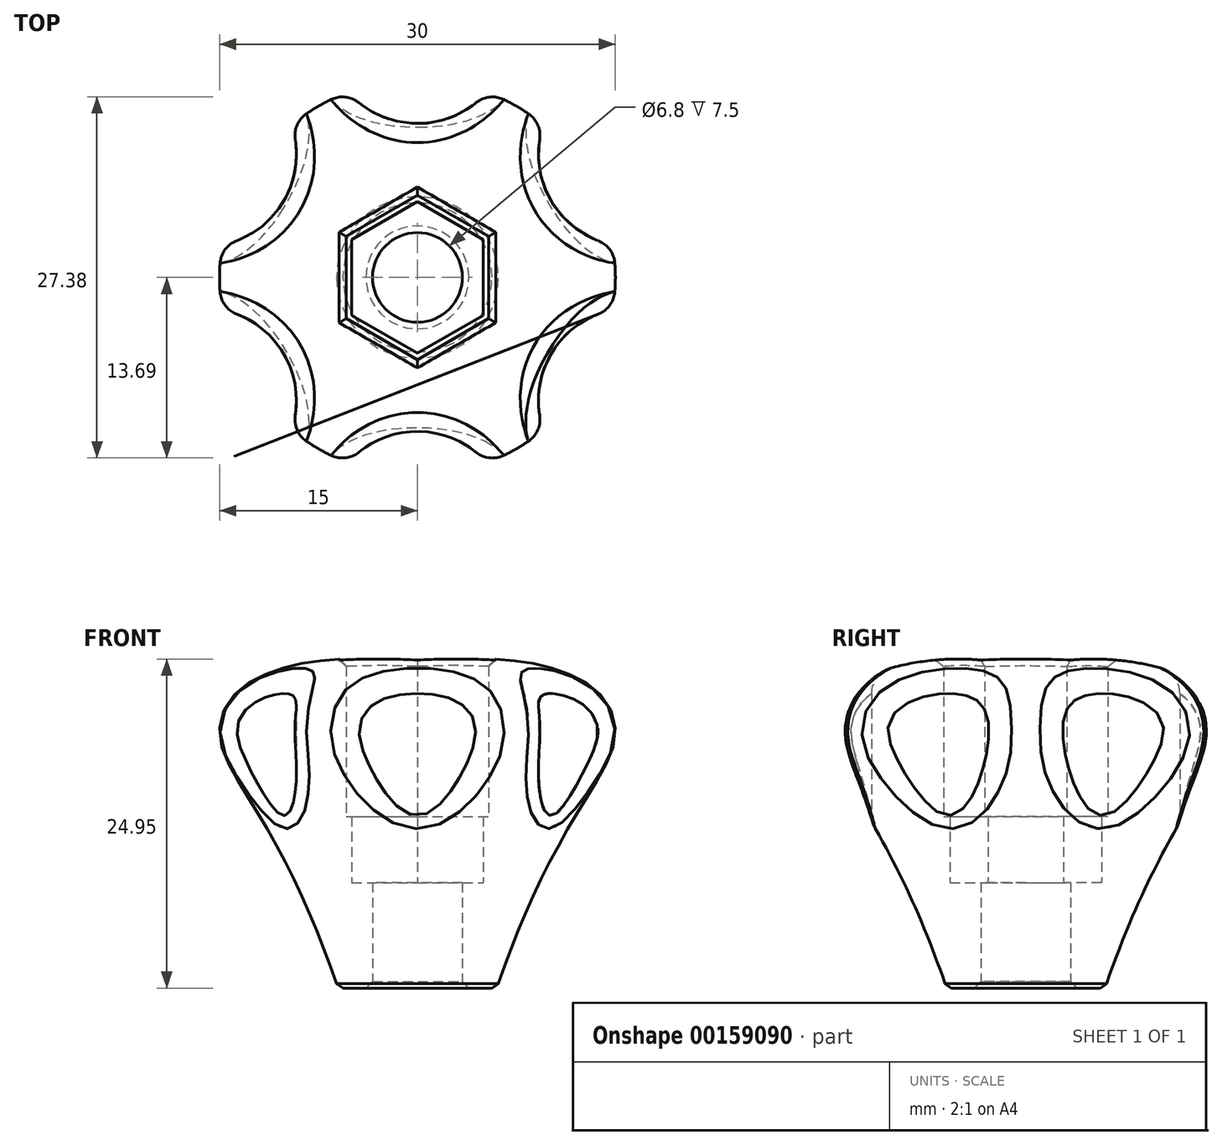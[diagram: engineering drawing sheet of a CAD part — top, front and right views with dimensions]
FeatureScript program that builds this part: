
annotation { "Feature Type Name" : "Feature", "Feature Type Description" : "" }
export const myFeature = defineFeature(function(context is Context, id is Id, definition is map)
    precondition{}
    {
        {
            var Q0;
            Q0=qCreatedBy(makeId("Right.planeOp"),FACE);
            var sketch = newSketch(context, id + "F0", { "sketchPlane" : qUnion([Q0])});
            skLineSegment(sketch, "E0", {"start": v(3.4, 25) * mm, "end": v(3.4, 0) * mm});
            skLineSegment(sketch, "E1", {"start": v(3.4, 0) * mm, "end": v(6, 0) * mm});
            skFitSpline(sketch, "E2", {"points": [v(6, 0) * mm, v(15, 19.47) * mm, v(3.4, 25) * mm], "startDerivative": vector(24.35, 70.88) * mm, "endDerivative": vector(-61.62, -0.98) * mm});
            skLineSegment(sketch, "E3", {"start": v(0, 0) * mm, "end": v(0, 25) * mm, "construction": true});
            skSolve(sketch);
        }
        {
            var Q0;
            Q0 = qSketchRegion(id + "F0", true);
            var Q1;
            Q1=sQuery(id+"F0.wireOp",EDGE,"E3");
            revolve(context, id + "F1", {"entities" : qUnion([Q0]), "axis" : qUnion([Q1]), "revolveType" : RevolveType.FULL});
        }
        {
            var Q0;
            Q0=qCreatedBy(makeId("Top.planeOp"),FACE);
            cPlane(context, id + "F2", {"entities" : qUnion([Q0]), "cplaneType" : CPlaneType.OFFSET, "offset" : 8 * mm, "width" : 150 * mm, "height" : 150 * mm});
        }
        {
            var Q0;
            Q0=qCreatedBy(id+"F2.planeOp",FACE);
            var sketch = newSketch(context, id + "F3", { "sketchPlane" : qUnion([Q0])});
            skCircle(sketch, "E4.cCircle", {"center": v(0, 0) * mm, "radius": 4.97 * mm, "construction": true});
            skLineSegment(sketch, "E4.0", {"start": v(0, 5.74) * mm, "end": v(4.98, 2.87) * mm});
            skLineSegment(sketch, "E4.1", {"start": v(4.97, 2.87) * mm, "end": v(4.97, -2.87) * mm});
            skLineSegment(sketch, "E4.2", {"start": v(4.97, -2.87) * mm, "end": v(0, -5.74) * mm});
            skLineSegment(sketch, "E4.3", {"start": v(0, -5.74) * mm, "end": v(-4.98, -2.87) * mm});
            skLineSegment(sketch, "E4.4", {"start": v(-4.97, -2.87) * mm, "end": v(-4.97, 2.87) * mm});
            skLineSegment(sketch, "E4.5", {"start": v(-4.97, 2.87) * mm, "end": v(0, 5.74) * mm});
            skPoint(sketch, "E4.0.midPoint", {"position": v(2.49, 4.3) * mm});
            skSolve(sketch);
        }
        {
            var Q0;
            Q0 = qSketchRegion(id + "F3", true);
            extrude(context, id + "F4", {"entities" : qUnion([Q0]), "operationType" : NewBodyOperationType.REMOVE, "depth" : 25 * mm});
        }
        {
            var Q0;
            Q0=qCreatedBy(id+"F2.planeOp",FACE);
            cPlane(context, id + "F5", {"entities" : qUnion([Q0]), "cplaneType" : CPlaneType.OFFSET, "offset" : 5 * mm, "width" : 150 * mm, "height" : 150 * mm});
        }
        {
            var Q0;
            Q0=qCreatedBy(id+"F5.planeOp",FACE);
            var sketch = newSketch(context, id + "F6", { "sketchPlane" : qUnion([Q0])});
            skFitSpline(sketch, "E5.1", {"points": [v(4.97, -2.87) * mm, v(4.97, -0.96) * mm, v(4.97, 0.96) * mm, v(4.97, 2.87) * mm], "construction": true});
            skFitSpline(sketch, "E5.2", {"points": [v(0, -5.74) * mm, v(1.66, -4.79) * mm, v(3.32, -3.83) * mm, v(4.97, -2.87) * mm], "construction": true});
            skFitSpline(sketch, "E5.5", {"points": [v(-4.97, -2.87) * mm, v(-3.32, -3.83) * mm, v(-1.66, -4.79) * mm, v(0, -5.74) * mm], "construction": true});
            skFitSpline(sketch, "E5.6", {"points": [v(-4.97, 2.87) * mm, v(-4.97, 0.96) * mm, v(-4.97, -0.96) * mm, v(-4.97, -2.87) * mm], "construction": true});
            skFitSpline(sketch, "E5.7", {"points": [v(0, 5.74) * mm, v(-1.66, 4.79) * mm, v(-3.32, 3.83) * mm, v(-4.97, 2.87) * mm], "construction": true});
            skLineSegment(sketch, "E5.13", {"start": v(0, 5.74) * mm, "end": v(4.97, 2.87) * mm, "construction": true});
            skCircle(sketch, "E6.cCircle", {"center": v(0, 0) * mm, "radius": 5.4 * mm, "construction": true});
            skLineSegment(sketch, "E6.0", {"start": v(5.4, 3.12) * mm, "end": v(5.4, -3.12) * mm});
            skLineSegment(sketch, "E6.1", {"start": v(5.4, -3.12) * mm, "end": v(0, -6.24) * mm});
            skLineSegment(sketch, "E6.2", {"start": v(0, -6.24) * mm, "end": v(-5.4, -3.12) * mm});
            skLineSegment(sketch, "E6.3", {"start": v(-5.4, -3.12) * mm, "end": v(-5.4, 3.12) * mm});
            skLineSegment(sketch, "E6.4", {"start": v(-5.4, 3.12) * mm, "end": v(0, 6.24) * mm});
            skLineSegment(sketch, "E6.5", {"start": v(0, 6.24) * mm, "end": v(5.4, 3.12) * mm});
            skPoint(sketch, "E6.0.midPoint", {"position": v(5.4, 0) * mm});
            skSolve(sketch);
        }
        {
            var Q0;
            Q0 = qSketchRegion(id + "F6", true);
            extrude(context, id + "F7", {"entities" : qUnion([Q0]), "operationType" : NewBodyOperationType.REMOVE, "depth" : 25 * mm});
        }
        {
            var Q0;
            Q0=makeQuery(id+"F7.boolean.opBoolean","INTERSECT",EDGE,{"derivedFrom":[makeQuery(id+"F1.opRevolve","SWEPT_FACE",FACE,{"disambiguationData":[OSD([sQuery(id+"F0.wireOp",EDGE,"E2")])]}),makeQuery(id+"F7.opExtrude","SWEPT_FACE",FACE,{"disambiguationData":[OSD([sQuery(id+"F6.wireOp",EDGE,"E6.0")])]})]});
            var Q1;
            Q1=makeQuery(id+"F7.boolean.opBoolean","INTERSECT",EDGE,{"derivedFrom":[makeQuery(id+"F1.opRevolve","SWEPT_FACE",FACE,{"disambiguationData":[OSD([sQuery(id+"F0.wireOp",EDGE,"E2")])]}),makeQuery(id+"F7.opExtrude","SWEPT_FACE",FACE,{"disambiguationData":[OSD([sQuery(id+"F6.wireOp",EDGE,"E6.5")])]})]});
            var Q2;
            Q2=makeQuery(id+"F7.boolean.opBoolean","INTERSECT",EDGE,{"derivedFrom":[makeQuery(id+"F1.opRevolve","SWEPT_FACE",FACE,{"disambiguationData":[OSD([sQuery(id+"F0.wireOp",EDGE,"E2")])]}),makeQuery(id+"F7.opExtrude","SWEPT_FACE",FACE,{"disambiguationData":[OSD([sQuery(id+"F6.wireOp",EDGE,"E6.4")])]})]});
            var Q3;
            Q3=makeQuery(id+"F7.boolean.opBoolean","INTERSECT",EDGE,{"derivedFrom":[makeQuery(id+"F1.opRevolve","SWEPT_FACE",FACE,{"disambiguationData":[OSD([sQuery(id+"F0.wireOp",EDGE,"E2")])]}),makeQuery(id+"F7.opExtrude","SWEPT_FACE",FACE,{"disambiguationData":[OSD([sQuery(id+"F6.wireOp",EDGE,"E6.3")])]})]});
            var Q4;
            Q4=makeQuery(id+"F7.boolean.opBoolean","INTERSECT",EDGE,{"derivedFrom":[makeQuery(id+"F1.opRevolve","SWEPT_FACE",FACE,{"disambiguationData":[OSD([sQuery(id+"F0.wireOp",EDGE,"E2")])]}),makeQuery(id+"F7.opExtrude","SWEPT_FACE",FACE,{"disambiguationData":[OSD([sQuery(id+"F6.wireOp",EDGE,"E6.2")])]})]});
            var Q5;
            Q5=makeQuery(id+"F7.boolean.opBoolean","INTERSECT",EDGE,{"derivedFrom":[makeQuery(id+"F1.opRevolve","SWEPT_FACE",FACE,{"disambiguationData":[OSD([sQuery(id+"F0.wireOp",EDGE,"E2")])]}),makeQuery(id+"F7.opExtrude","SWEPT_FACE",FACE,{"disambiguationData":[OSD([sQuery(id+"F6.wireOp",EDGE,"E6.1")])]})]});
            var Q6;
            Q6=makeQuery(id+"F1.opRevolve","SWEPT_EDGE",EDGE,{"disambiguationData":[OSD([sQuery(id+"F0.wireOp",EDGE,"E0"),sQuery(id+"F0.wireOp",EDGE,"E1")])]});
            var Q7;
            Q7=makeQuery(id+"F1.opRevolve","SWEPT_EDGE",EDGE,{"disambiguationData":[OSD([sQuery(id+"F0.wireOp",EDGE,"E1"),sQuery(id+"F0.wireOp",EDGE,"E2")])]});
            chamfer(context, id + "F8", {"entities" : qUnion([Q0, Q1, Q2, Q3, Q4, Q5, Q6, Q7]), "width" : 0.5 * mm, "tangentPropagation" : true});
        }
        {
            var Q0;
            Q0=qCreatedBy(makeId("Top.planeOp"),FACE);
            var sketch = newSketch(context, id + "F9", { "sketchPlane" : qUnion([Q0])});
            skCircle(sketch, "E7", {"center": v(0, 18.67) * mm, "radius": 7 * mm});
            skCircle(sketch, "E8.1.0", {"center": v(-16.17, 9.34) * mm, "radius": 7 * mm});
            skCircle(sketch, "E8.2.0", {"center": v(-16.17, -9.34) * mm, "radius": 7 * mm});
            skCircle(sketch, "E8.3.0", {"center": v(0, -18.67) * mm, "radius": 7 * mm});
            skCircle(sketch, "E8.4.0", {"center": v(16.17, -9.34) * mm, "radius": 7 * mm});
            skCircle(sketch, "E8.5.0", {"center": v(16.17, 9.34) * mm, "radius": 7 * mm});
            skPoint(sketch, "E8.center", {"position": v(0, 0) * mm});
            skSolve(sketch);
        }
        {
            var Q0;
            Q0 = qSketchRegion(id + "F9", true);
            extrude(context, id + "F10", {"entities" : qUnion([Q0]), "operationType" : NewBodyOperationType.REMOVE, "depth" : 25 * mm});
        }
        {
            var Q0;
            Q0=makeQuery(id+"F10.boolean.opBoolean","COPY",FACE,{"derivedFrom":makeQuery(id+"F10.opExtrude","SWEPT_FACE",FACE,{"disambiguationData":[OSD([sQuery(id+"F9.wireOp",EDGE,"E8.3.0")])]})});
            var Q1;
            Q1=makeQuery(id+"F10.boolean.opBoolean","COPY",FACE,{"derivedFrom":makeQuery(id+"F10.opExtrude","SWEPT_FACE",FACE,{"disambiguationData":[OSD([sQuery(id+"F9.wireOp",EDGE,"E8.4.0")])]})});
            var Q2;
            Q2=makeQuery(id+"F10.boolean.opBoolean","COPY",FACE,{"derivedFrom":makeQuery(id+"F10.opExtrude","SWEPT_FACE",FACE,{"disambiguationData":[OSD([sQuery(id+"F9.wireOp",EDGE,"E8.5.0")])]})});
            var Q3;
            Q3=makeQuery(id+"F10.boolean.opBoolean","COPY",FACE,{"derivedFrom":makeQuery(id+"F10.opExtrude","SWEPT_FACE",FACE,{"disambiguationData":[OSD([sQuery(id+"F9.wireOp",EDGE,"E8.2.0")])]})});
            var Q4;
            Q4=makeQuery(id+"F10.boolean.opBoolean","COPY",FACE,{"derivedFrom":makeQuery(id+"F10.opExtrude","SWEPT_FACE",FACE,{"disambiguationData":[OSD([sQuery(id+"F9.wireOp",EDGE,"E8.1.0")])]})});
            var Q5;
            Q5=makeQuery(id+"F10.boolean.opBoolean","COPY",FACE,{"derivedFrom":makeQuery(id+"F10.opExtrude","SWEPT_FACE",FACE,{"disambiguationData":[OSD([sQuery(id+"F9.wireOp",EDGE,"E7")])]})});
            fillet(context, id + "F11", {"entities" : qUnion([Q0, Q1, Q2, Q3, Q4, Q5]), "radius" : 2 * mm, "tangentPropagation" : true, "allowEdgeOverflow" : false});
        }
    });
